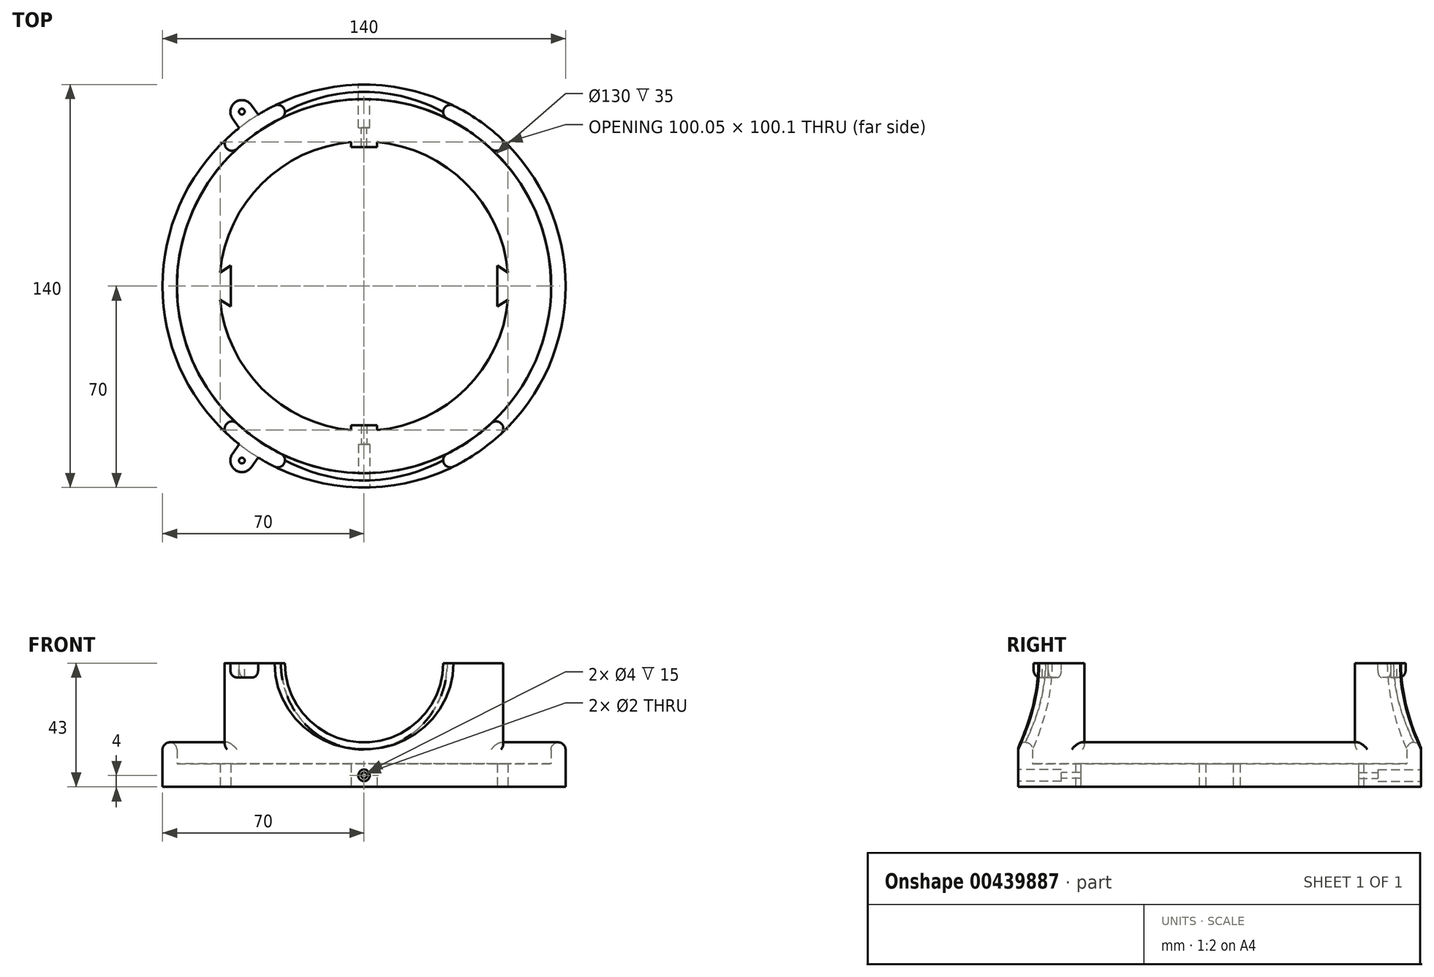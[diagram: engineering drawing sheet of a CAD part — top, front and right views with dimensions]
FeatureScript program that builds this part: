
annotation { "Feature Type Name" : "Feature", "Feature Type Description" : "" }
export const myFeature = defineFeature(function(context is Context, id is Id, definition is map)
    precondition{}
    {
        {
            var Q0;
            Q0=qCreatedBy(makeId("Top.planeOp"),FACE);
            var sketch = newSketch(context, id + "F0", { "sketchPlane" : qUnion([Q0])});
            skArc(sketch, "E0", {"start": v(-50.02, -4.77) * mm, "mid": v(-35.44, -35.63) * mm, "end": v(-4.5, -50.05) * mm});
            skCircle(sketch, "E1", {"center": v(0, 0) * mm, "radius": 70 * mm});
            skLineSegment(sketch, "E2.2.0.2", {"start": v(4.5, 50.05) * mm, "end": v(4.5, 48.3) * mm});
            skLineSegment(sketch, "E2.2.0.3", {"start": v(-4.5, 50.05) * mm, "end": v(-4.5, 48.3) * mm});
            skArc(sketch, "E3.trimOffspring", {"start": v(-4.5, 50.05) * mm, "mid": v(-35.44, 35.63) * mm, "end": v(-50.02, 4.77) * mm});
            skLineSegment(sketch, "E4", {"start": v(-4.5, 48.3) * mm, "end": v(4.5, 48.3) * mm});
            skLineSegment(sketch, "E5.MirrorCS", {"start": v(-4.5, -50.05) * mm, "end": v(-4.5, -48.3) * mm});
            skLineSegment(sketch, "E6.MirrorCS", {"start": v(4.5, -50.05) * mm, "end": v(4.5, -48.3) * mm});
            skLineSegment(sketch, "E7.MirrorCS", {"start": v(-4.5, -48.3) * mm, "end": v(4.5, -48.3) * mm});
            skLineSegment(sketch, "E8", {"start": v(-46.3, 7.1) * mm, "end": v(-46.3, -7.1) * mm});
            skLineSegment(sketch, "E9", {"start": v(-50.02, -4.77) * mm, "end": v(-46.3, -7.1) * mm});
            skLineSegment(sketch, "E10", {"start": v(-50.02, 4.77) * mm, "end": v(-46.3, 7.1) * mm});
            skLineSegment(sketch, "E11.MirrorCS", {"start": v(50.02, -4.77) * mm, "end": v(46.3, -7.1) * mm});
            skLineSegment(sketch, "E12.MirrorCS", {"start": v(50.02, 4.77) * mm, "end": v(46.3, 7.1) * mm});
            skLineSegment(sketch, "E13.MirrorCS", {"start": v(46.3, 7.1) * mm, "end": v(46.3, -7.1) * mm});
            skArc(sketch, "E14.MirrorCS", {"start": v(4.5, 50.05) * mm, "mid": v(35.44, 35.63) * mm, "end": v(50.02, 4.77) * mm});
            skArc(sketch, "E15.MirrorCS", {"start": v(50.02, -4.77) * mm, "mid": v(35.44, -35.63) * mm, "end": v(4.5, -50.05) * mm});
            skSolve(sketch);
        }
        {
            var Q0;
            Q0=qSketchRegion(id+"F0",true);
            extrude(context, id + "F1", {"entities" : qUnion([Q0]), "depth" : 43 * mm});
        }
        {
            var Q0;
            Q0=qCreatedBy(makeId("Front.planeOp"),FACE);
            var sketch = newSketch(context, id + "F2", { "sketchPlane" : qUnion([Q0])});
            skCircle(sketch, "E16", {"center": v(0, 43) * mm, "radius": 27.5 * mm});
            skLineSegment(sketch, "E17", {"start": v(0, 0) * mm, "end": v(0, 43) * mm});
            skSolve(sketch);
        }
        {
            var Q0;
            Q0=qSketchRegion(id+"F2",true);
            extrude(context, id + "F3", {"entities" : qUnion([Q0]), "operationType" : NewBodyOperationType.REMOVE, "endBound" : BoundingType.SYMMETRIC, "oppositeDirection" : true, "depth" : 162.8 * mm});
        }
        {
            var Q0;
            Q0=makeQuery(id+"F1.opExtrude","CAP_FACE",FACE,{"disambiguationData":[OSD([sQuery(id+"F0.wireOp",EDGE,"E0"),sQuery(id+"F0.wireOp",EDGE,"E1"),sQuery(id+"F0.wireOp",EDGE,"KXo9hoNV-a9ZN-jEZJ-Yrdq-8QQVipn73RV8.bottom"),sQuery(id+"F0.wireOp",EDGE,"KXo9hoNV-a9ZN-jEZJ-Yrdq-8QQVipn73RV8.top"),sQuery(id+"F0.wireOp",EDGE,"KXo9hoNV-a9ZN-jEZJ-Yrdq-8QQVipn73RV8.right"),sQuery(id+"F0.wireOp",EDGE,"E2.1.0.1"),sQuery(id+"F0.wireOp",EDGE,"E2.1.0.2"),sQuery(id+"F0.wireOp",EDGE,"E2.1.0.3"),sQuery(id+"F0.wireOp",EDGE,"E2.2.0.0"),sQuery(id+"F0.wireOp",EDGE,"E2.2.0.2"),sQuery(id+"F0.wireOp",EDGE,"E2.2.0.3"),sQuery(id+"F0.wireOp",EDGE,"E2.3.0.1"),sQuery(id+"F0.wireOp",EDGE,"E2.3.0.2"),sQuery(id+"F0.wireOp",EDGE,"E2.3.0.3"),sQuery(id+"F0.wireOp",EDGE,"085ecb79-89d6-48a0-bd8e-482740248965.trimOffspring"),sQuery(id+"F0.wireOp",EDGE,"85cd406b-6394-40b1-ac36-b08ea9fcf00d.trimOffspring"),sQuery(id+"F0.wireOp",EDGE,"E3.trimOffspring")])],"isStart":false});
            var sketch = newSketch(context, id + "F4", { "sketchPlane" : qUnion([Q0])});
            skLineSegment(sketch, "E18", {"start": v(-70, 0) * mm, "end": v(70, 0) * mm, "construction": true});
            skLineSegment(sketch, "E19", {"start": v(60.95, -87.04) * mm, "end": v(0, 0) * mm, "construction": true});
            skLineSegment(sketch, "E20", {"start": v(-59.95, -85.62) * mm, "end": v(0, 0) * mm, "construction": true});
            skLineSegment(sketch, "E21", {"start": v(-55.05, 78.61) * mm, "end": v(0, 0) * mm, "construction": true});
            skLineSegment(sketch, "E22", {"start": v(60.26, 86.06) * mm, "end": v(0, 0) * mm, "construction": true});
            skCircle(sketch, "E23", {"center": v(-42.44, -60.62) * mm, "radius": 1 * mm, "construction": true});
            skCircle(sketch, "E24", {"center": v(0, 0) * mm, "radius": 70 * mm, "construction": true});
            skLineSegment(sketch, "E25", {"start": v(0, 68.4) * mm, "end": v(0, -71.35) * mm, "construction": true});
            skCircle(sketch, "E26.MirrorC", {"center": v(42.44, -60.62) * mm, "radius": 1 * mm, "construction": true});
            skCircle(sketch, "E27.MirrorC", {"center": v(42.44, 60.62) * mm, "radius": 1 * mm, "construction": true});
            skLineSegment(sketch, "E28.MirrorCS", {"start": v(39.17, 62.91) * mm, "end": v(36.68, 59.61) * mm});
            skCircle(sketch, "E29.MirrorC", {"center": v(-42.44, 60.62) * mm, "radius": 1 * mm, "construction": true});
            skArc(sketch, "E30", {"start": v(45.72, 58.32) * mm, "mid": v(44.74, 63.9) * mm, "end": v(39.17, 62.91) * mm});
            skLineSegment(sketch, "E31.MirrorCS", {"start": v(45.72, 58.32) * mm, "end": v(43.47, 54.86) * mm});
            skArc(sketch, "E32", {"start": v(-39.17, 62.91) * mm, "mid": v(-44.74, 63.9) * mm, "end": v(-45.72, 58.32) * mm});
            skLineSegment(sketch, "E33", {"start": v(-45.72, 58.32) * mm, "end": v(-43.36, 54.95) * mm});
            skLineSegment(sketch, "E34.MirrorCS", {"start": v(-39.17, 62.91) * mm, "end": v(-36.8, 59.54) * mm});
            skArc(sketch, "E35", {"start": v(39.17, -62.91) * mm, "mid": v(44.74, -63.9) * mm, "end": v(45.72, -58.32) * mm});
            skLineSegment(sketch, "E36", {"start": v(45.72, -58.32) * mm, "end": v(43.36, -54.95) * mm});
            skLineSegment(sketch, "E37.MirrorCS", {"start": v(39.17, -62.91) * mm, "end": v(36.8, -59.54) * mm});
            skArc(sketch, "E38", {"start": v(-45.72, -58.32) * mm, "mid": v(-44.74, -63.9) * mm, "end": v(-39.17, -62.91) * mm});
            skLineSegment(sketch, "E39", {"start": v(-45.72, -58.32) * mm, "end": v(-43.36, -54.95) * mm});
            skLineSegment(sketch, "E40.MirrorCS", {"start": v(-39.17, -62.91) * mm, "end": v(-36.8, -59.54) * mm});
            skSolve(sketch);
        }
        {
            var Q0;
            Q0=qSketchRegion(id+"F2",true);
            extrude(context, id + "F5", {"entities" : qUnion([Q0]), "operationType" : NewBodyOperationType.REMOVE, "endBound" : BoundingType.SYMMETRIC, "oppositeDirection" : true, "depth" : 172.6 * mm});
        }
        {
            var Q0;
            Q0=qCreatedBy(makeId("Right.planeOp"),FACE);
            var sketch = newSketch(context, id + "F6", { "sketchPlane" : qUnion([Q0])});
            skLineSegment(sketch, "E41.bottom", {"start": v(-47, 115.5) * mm, "end": v(47, 115.5) * mm});
            skLineSegment(sketch, "E41.top", {"start": v(-47, 15.5) * mm, "end": v(47, 15.5) * mm});
            skLineSegment(sketch, "E41.left", {"start": v(-47, 115.5) * mm, "end": v(-47, 15.5) * mm});
            skLineSegment(sketch, "E41.right", {"start": v(47, 115.5) * mm, "end": v(47, 15.5) * mm});
            skLineSegment(sketch, "E42", {"start": v(0, 0) * mm, "end": v(0, 15.5) * mm, "construction": true});
            skSolve(sketch);
        }
        {
            var Q0;
            Q0=qSketchRegion(id+"F6",true);
            extrude(context, id + "F7", {"entities" : qUnion([Q0]), "operationType" : NewBodyOperationType.REMOVE, "endBound" : BoundingType.SYMMETRIC, "depth" : 182.4 * mm});
        }
        {
            var Q0;
            Q0=makeQuery(id+"F1.opExtrude","CAP_FACE",FACE,{"disambiguationData":[OSD([sQuery(id+"F0.wireOp",EDGE,"E0"),sQuery(id+"F0.wireOp",EDGE,"E1"),sQuery(id+"F0.wireOp",EDGE,"E2.2.0.0"),sQuery(id+"F0.wireOp",EDGE,"E2.2.0.2"),sQuery(id+"F0.wireOp",EDGE,"E2.2.0.3"),sQuery(id+"F0.wireOp",EDGE,"E2.3.0.1"),sQuery(id+"F0.wireOp",EDGE,"E2.3.0.2"),sQuery(id+"F0.wireOp",EDGE,"E2.3.0.3"),sQuery(id+"F0.wireOp",EDGE,"085ecb79-89d6-48a0-bd8e-482740248965.trimOffspring"),sQuery(id+"F0.wireOp",EDGE,"85cd406b-6394-40b1-ac36-b08ea9fcf00d.trimOffspring"),sQuery(id+"F0.wireOp",EDGE,"E3.trimOffspring"),sQuery(id+"F0.wireOp",EDGE,"0wMoWTtO-hKPG-dmUJ-9eZK-Rki3Ka56Pj0p"),sQuery(id+"F0.wireOp",EDGE,"V7nILoa6-agM4-B80q-80k6-MabAC6LeFQ3d"),sQuery(id+"F0.wireOp",EDGE,"T4tWseir-YMXC-WR8s-1T1N-fBKYRdHiWXzI"),sQuery(id+"F0.wireOp",EDGE,"GhSFunWE-UcgT-IK5w-9III-MmuMwgvZ9d2i"),sQuery(id+"F0.wireOp",EDGE,"6XujKZao-lyGk-p0ZG-WLlf-O7pdLShlOZ0q"),sQuery(id+"F0.wireOp",EDGE,"wTnajsCB-XfUZ-x2k5-9YjB-GDWOXe4ybcG3")])],"isStart":true});
            cPlane(context, id + "F8", {"entities" : qUnion([Q0]), "cplaneType" : CPlaneType.OFFSET, "offset" : 8 * mm, "oppositeDirection" : true, "width" : 150 * mm, "height" : 150 * mm});
        }
        {
            var Q0;
            Q0=qCreatedBy(id+"F8.planeOp",FACE);
            var sketch = newSketch(context, id + "F9", { "sketchPlane" : qUnion([Q0])});
            skCircle(sketch, "E43", {"center": v(0, 0) * mm, "radius": 50.25 * mm});
            skSolve(sketch);
        }
        {
            var Q0;
            Q0=qSketchRegion(id+"F9",true);
            var Q1;
            Q1=sQuery(id+"F9.wireOp",EDGE,"E43");
            extrude(context, id + "F10", {"entities" : qUnion([Q0]), "operationType" : NewBodyOperationType.REMOVE, "surfaceEntities" : qUnion([Q1]), "oppositeDirection" : true, "depth" : 73.1 * mm});
        }
        {
            var Q0;
            Q0=makeQuery(id+"F4.imprint","IMPRINT",FACE,{"disambiguationData":[TD([[makeQuery(id+"F4.imprint","IMPRINT",EDGE,{"derivedFrom":sQuery(id+"F4.wireOp",EDGE,"E32")}),1.0]])]});
            var Q1;
            {var subQ0=sQuery(id+"F4.wireOp",EDGE,"E30");Q1=makeQuery(id+"F4.imprint","IMPRINT",FACE,{"disambiguationData":[TD([[makeQuery(id+"F4.imprint","IMPRINT",EDGE,{"derivedFrom":subQ0}),1.0]])]});}
            var Q2;
            Q2=makeQuery(id+"F4.imprint","IMPRINT",FACE,{"disambiguationData":[TD([[makeQuery(id+"F4.imprint","IMPRINT",EDGE,{"derivedFrom":sQuery(id+"F4.wireOp",EDGE,"E35")}),1.0]])]});
            var Q3;
            Q3=makeQuery(id+"F4.imprint","IMPRINT",FACE,{"disambiguationData":[TD([[makeQuery(id+"F4.imprint","IMPRINT",EDGE,{"derivedFrom":sQuery(id+"F4.wireOp",EDGE,"E38")}),1.0]])]});
            extrude(context, id + "F11", {"entities" : qUnion([Q0, Q1, Q2, Q3]), "operationType" : NewBodyOperationType.ADD, "oppositeDirection" : true, "depth" : 5 * mm});
        }
        {
            var Q0;
            Q0=sQuery(id+"F4.wireOp",VERTEX,"E29.MirrorC.center");
            var Q1;
            Q1=sQuery(id+"F4.wireOp",VERTEX,"E30.center");
            var Q2;
            Q2=sQuery(id+"F4.wireOp",VERTEX,"E35.center");
            var Q3;
            Q3=sQuery(id+"F4.wireOp",VERTEX,"E23.center");
            var Q4;
            Q4=makeQuery(id+"F1.opExtrude","SWEPT_BODY",BODY,{"disambiguationData":[OSD([sQuery(id+"F0.wireOp",EDGE,"E0"),sQuery(id+"F0.wireOp",EDGE,"E1"),sQuery(id+"F0.wireOp",EDGE,"E2.2.0.2"),sQuery(id+"F0.wireOp",EDGE,"E2.2.0.3"),sQuery(id+"F0.wireOp",EDGE,"085ecb79-89d6-48a0-bd8e-482740248965.trimOffspring"),sQuery(id+"F0.wireOp",EDGE,"85cd406b-6394-40b1-ac36-b08ea9fcf00d.trimOffspring"),sQuery(id+"F0.wireOp",EDGE,"E3.trimOffspring"),sQuery(id+"F0.wireOp",EDGE,"wPdThzp9-JF6t-tdpl-VHkU-ta3l5vbWA5lS"),sQuery(id+"F0.wireOp",EDGE,"bCEz1Pkn-wXIZ-K7jB-S2CN-AWV0JzSdVKlh"),sQuery(id+"F0.wireOp",EDGE,"JKQ4kFbc-aIyo-4Fwi-89Tz-roniWSClhzpP"),sQuery(id+"F0.wireOp",EDGE,"de4d509a-07cf-4a36-b25b-d70c5453503e0.MirrorCS"),sQuery(id+"F0.wireOp",EDGE,"de4d509a-07cf-4a36-b25b-d70c5453503e1.MirrorCS"),sQuery(id+"F0.wireOp",EDGE,"de4d509a-07cf-4a36-b25b-d70c5453503e2.MirrorCS"),sQuery(id+"F0.wireOp",EDGE,"E4"),sQuery(id+"F0.wireOp",EDGE,"E5.MirrorCS"),sQuery(id+"F0.wireOp",EDGE,"E6.MirrorCS"),sQuery(id+"F0.wireOp",EDGE,"E7.MirrorCS")])]});
            hole(context, id + "F12", {"style" : HoleStyle.SIMPLE, "endStyle" : HoleEndStyle.BLIND, "holeDiameter" : 2 * mm, "holeDepth" : 5 * mm, "isTappedThrough" : true, "tappedDepth" : 12 * mm, "tapClearance" : 3, "startFromSketch" : true, "locations" : qUnion([Q0, Q1, Q2, Q3]), "scope" : qUnion([Q4])});
        }
        {
            var Q0;
            Q0=qCreatedBy(makeId("Top.planeOp"),FACE);
            cPlane(context, id + "F13", {"entities" : qUnion([Q0]), "cplaneType" : CPlaneType.OFFSET, "offset" : 8 * mm, "width" : 150 * mm, "height" : 150 * mm});
        }
        {
            var Q0;
            Q0=qCreatedBy(id+"F13.planeOp",FACE);
            var sketch = newSketch(context, id + "F14", { "sketchPlane" : qUnion([Q0])});
            skCircle(sketch, "E44", {"center": v(0, 0) * mm, "radius": 65 * mm});
            skCircle(sketch, "E45", {"center": v(0, 0) * mm, "radius": 50.25 * mm});
            skSolve(sketch);
        }
        {
            var Q0;
            Q0 = qSketchRegion(id + "F14", true);
            extrude(context, id + "F15", {"entities" : qUnion([Q0]), "operationType" : NewBodyOperationType.REMOVE, "depth" : 63.8 * mm});
        }
        {
            var Q0;
            Q0=makeQuery(id+"F7.boolean.opBoolean","INTERSECT",EDGE,{"disambiguationData":[OD(1.0)],"derivedFrom":[makeQuery(id+"F1.opExtrude","SWEPT_FACE",FACE,{"disambiguationData":[OSD([sQuery(id+"F0.wireOp",EDGE,"E1")])]}),makeQuery(id+"F7.opExtrude","SWEPT_FACE",FACE,{"disambiguationData":[OSD([sQuery(id+"F6.wireOp",EDGE,"E41.top")])]})]});
            var Q1;
            Q1=makeQuery(id+"F7.boolean.opBoolean","INTERSECT",EDGE,{"disambiguationData":[OD(0.0)],"derivedFrom":[makeQuery(id+"F1.opExtrude","SWEPT_FACE",FACE,{"disambiguationData":[OSD([sQuery(id+"F0.wireOp",EDGE,"E1")])]}),makeQuery(id+"F7.opExtrude","SWEPT_FACE",FACE,{"disambiguationData":[OSD([sQuery(id+"F6.wireOp",EDGE,"E41.top")])]})]});
            var Q2;
            Q2=makeQuery(id+"F3.boolean.opBoolean","INTERSECT",EDGE,{"disambiguationData":[OD(0.0)],"derivedFrom":[makeQuery(id+"F1.opExtrude","SWEPT_FACE",FACE,{"disambiguationData":[OSD([sQuery(id+"F0.wireOp",EDGE,"E1")])]}),makeQuery(id+"F3.opExtrude","SWEPT_FACE",FACE,{"disambiguationData":[OSD([sQuery(id+"F2.wireOp",EDGE,"E16")])]})]});
            var Q3;
            Q3=makeQuery(id+"F3.boolean.opBoolean","INTERSECT",EDGE,{"disambiguationData":[OD(1.0)],"derivedFrom":[makeQuery(id+"F1.opExtrude","SWEPT_FACE",FACE,{"disambiguationData":[OSD([sQuery(id+"F0.wireOp",EDGE,"E1")])]}),makeQuery(id+"F3.opExtrude","SWEPT_FACE",FACE,{"disambiguationData":[OSD([sQuery(id+"F2.wireOp",EDGE,"E16")])]})]});
            var Q4;
            {var subQ5=sQuery(id+"F0.wireOp",EDGE,"E0");Q4=makeQuery(id+"F15.boolean.opBoolean","INTERSECT",EDGE,{"derivedFrom":[makeQuery(id+"F3.boolean.opBoolean","COPY",FACE,{"disambiguationData":[TD([makeQuery(id+"F1.opExtrude","SWEPT_FACE",FACE,{"disambiguationData":[OSD([subQ5])]})])],"derivedFrom":makeQuery(id+"F3.opExtrude","SWEPT_FACE",FACE,{"disambiguationData":[OSD([sQuery(id+"F2.wireOp",EDGE,"E16")])]})}),makeQuery(id+"F15.opExtrude","SWEPT_FACE",FACE,{"disambiguationData":[OSD([sQuery(id+"F14.wireOp",EDGE,"E44")])]})]});}
            var Q5;
            {var subQ1=sQuery(id+"F0.wireOp",EDGE,"E2.2.0.2");Q5=makeQuery(id+"F15.boolean.opBoolean","INTERSECT",EDGE,{"derivedFrom":[makeQuery(id+"F3.boolean.opBoolean","COPY",FACE,{"disambiguationData":[TD([makeQuery(id+"F1.opExtrude","SWEPT_FACE",FACE,{"disambiguationData":[OSD([subQ1])]})])],"derivedFrom":makeQuery(id+"F3.opExtrude","SWEPT_FACE",FACE,{"disambiguationData":[OSD([sQuery(id+"F2.wireOp",EDGE,"E16")])]})}),makeQuery(id+"F15.opExtrude","SWEPT_FACE",FACE,{"disambiguationData":[OSD([sQuery(id+"F14.wireOp",EDGE,"E44")])]})]});}
            var Q6;
            Q6=makeQuery(id+"F15.boolean.opBoolean","INTERSECT",EDGE,{"derivedFrom":[makeQuery(id+"F7.boolean.opBoolean","COPY",FACE,{"disambiguationData":[TD([makeQuery(id+"F1.opExtrude","SWEPT_FACE",FACE,{"disambiguationData":[OSD([sQuery(id+"F0.wireOp",EDGE,"E11.MirrorCS")])]})])],"derivedFrom":makeQuery(id+"F7.opExtrude","SWEPT_FACE",FACE,{"disambiguationData":[OSD([sQuery(id+"F6.wireOp",EDGE,"E41.top")])]})}),makeQuery(id+"F15.opExtrude","SWEPT_FACE",FACE,{"disambiguationData":[OSD([sQuery(id+"F14.wireOp",EDGE,"E44")])]})]});
            var Q7;
            Q7=makeQuery(id+"F15.boolean.opBoolean","INTERSECT",EDGE,{"derivedFrom":[makeQuery(id+"F7.boolean.opBoolean","COPY",FACE,{"disambiguationData":[TD([makeQuery(id+"F1.opExtrude","SWEPT_FACE",FACE,{"disambiguationData":[OSD([sQuery(id+"F0.wireOp",EDGE,"E0")])]})])],"derivedFrom":makeQuery(id+"F7.opExtrude","SWEPT_FACE",FACE,{"disambiguationData":[OSD([sQuery(id+"F6.wireOp",EDGE,"E41.top")])]})}),makeQuery(id+"F15.opExtrude","SWEPT_FACE",FACE,{"disambiguationData":[OSD([sQuery(id+"F14.wireOp",EDGE,"E44")])]})]});
            fillet(context, id + "F16", {"entities" : qUnion([Q0, Q1, Q2, Q3, Q4, Q5, Q6, Q7]), "radius" : 2.5 * mm, "tangentPropagation" : true, "allowEdgeOverflow" : false});
        }
        {
            var Q0;
            {var subQ3=sQuery(id+"F0.wireOp",EDGE,"E15.MirrorCS");var subQ8=makeQuery(id+"F1.opExtrude","SWEPT_FACE",FACE,{"disambiguationData":[OSD([subQ3])]});Q0=makeQuery(id+"F15.boolean.opBoolean","INTERSECT",EDGE,{"derivedFrom":[makeQuery(id+"F7.boolean.opBoolean","COPY",FACE,{"disambiguationData":[TD([subQ8])],"derivedFrom":makeQuery(id+"F7.opExtrude","SWEPT_FACE",FACE,{"disambiguationData":[OSD([sQuery(id+"F6.wireOp",EDGE,"E41.left")])]})}),makeQuery(id+"F15.opExtrude","SWEPT_FACE",FACE,{"disambiguationData":[OSD([sQuery(id+"F14.wireOp",EDGE,"E44")])]})]});}
            var Q1;
            {var subQ4=sQuery(id+"F0.wireOp",EDGE,"E14.MirrorCS");var subQ8=makeQuery(id+"F1.opExtrude","SWEPT_FACE",FACE,{"disambiguationData":[OSD([subQ4])]});Q1=makeQuery(id+"F15.boolean.opBoolean","INTERSECT",EDGE,{"derivedFrom":[makeQuery(id+"F7.boolean.opBoolean","COPY",FACE,{"disambiguationData":[TD([subQ8])],"derivedFrom":makeQuery(id+"F7.opExtrude","SWEPT_FACE",FACE,{"disambiguationData":[OSD([sQuery(id+"F6.wireOp",EDGE,"E41.right")])]})}),makeQuery(id+"F15.opExtrude","SWEPT_FACE",FACE,{"disambiguationData":[OSD([sQuery(id+"F14.wireOp",EDGE,"E44")])]})]});}
            var Q2;
            {var subQ5=sQuery(id+"F0.wireOp",EDGE,"E0");Q2=makeQuery(id+"F15.boolean.opBoolean","INTERSECT",EDGE,{"derivedFrom":[makeQuery(id+"F3.boolean.opBoolean","COPY",FACE,{"disambiguationData":[TD([makeQuery(id+"F1.opExtrude","SWEPT_FACE",FACE,{"disambiguationData":[OSD([subQ5])]})])],"derivedFrom":makeQuery(id+"F3.opExtrude","SWEPT_FACE",FACE,{"disambiguationData":[OSD([sQuery(id+"F2.wireOp",EDGE,"E16")])]})}),makeQuery(id+"F15.opExtrude","SWEPT_FACE",FACE,{"disambiguationData":[OSD([sQuery(id+"F14.wireOp",EDGE,"E44")])]})]});}
            var Q3;
            Q3=makeQuery(id+"F7.boolean.opBoolean","INTERSECT",EDGE,{"disambiguationData":[OD(1.0)],"derivedFrom":[makeQuery(id+"F1.opExtrude","SWEPT_FACE",FACE,{"disambiguationData":[OSD([sQuery(id+"F0.wireOp",EDGE,"E1")])]}),makeQuery(id+"F7.opExtrude","SWEPT_FACE",FACE,{"disambiguationData":[OSD([sQuery(id+"F6.wireOp",EDGE,"E41.right")])]})]});
            var Q4;
            Q4=makeQuery(id+"F7.boolean.opBoolean","INTERSECT",EDGE,{"disambiguationData":[OD(1.0)],"derivedFrom":[makeQuery(id+"F1.opExtrude","SWEPT_FACE",FACE,{"disambiguationData":[OSD([sQuery(id+"F0.wireOp",EDGE,"E1")])]}),makeQuery(id+"F7.opExtrude","SWEPT_FACE",FACE,{"disambiguationData":[OSD([sQuery(id+"F6.wireOp",EDGE,"E41.left")])]})]});
            var Q5;
            Q5=makeQuery(id+"F7.boolean.opBoolean","INTERSECT",EDGE,{"disambiguationData":[OD(0.0)],"derivedFrom":[makeQuery(id+"F1.opExtrude","SWEPT_FACE",FACE,{"disambiguationData":[OSD([sQuery(id+"F0.wireOp",EDGE,"E1")])]}),makeQuery(id+"F7.opExtrude","SWEPT_FACE",FACE,{"disambiguationData":[OSD([sQuery(id+"F6.wireOp",EDGE,"E41.left")])]})]});
            var Q6;
            Q6=makeQuery(id+"F7.boolean.opBoolean","INTERSECT",EDGE,{"disambiguationData":[OD(0.0)],"derivedFrom":[makeQuery(id+"F1.opExtrude","SWEPT_FACE",FACE,{"disambiguationData":[OSD([sQuery(id+"F0.wireOp",EDGE,"E1")])]}),makeQuery(id+"F7.opExtrude","SWEPT_FACE",FACE,{"disambiguationData":[OSD([sQuery(id+"F6.wireOp",EDGE,"E41.right")])]})]});
            var Q7;
            {var subQ6=sQuery(id+"F0.wireOp",EDGE,"E0");var subQ8=makeQuery(id+"F1.opExtrude","SWEPT_FACE",FACE,{"disambiguationData":[OSD([subQ6])]});Q7=makeQuery(id+"F15.boolean.opBoolean","INTERSECT",EDGE,{"derivedFrom":[makeQuery(id+"F7.boolean.opBoolean","COPY",FACE,{"disambiguationData":[TD([subQ8])],"derivedFrom":makeQuery(id+"F7.opExtrude","SWEPT_FACE",FACE,{"disambiguationData":[OSD([sQuery(id+"F6.wireOp",EDGE,"E41.left")])]})}),makeQuery(id+"F15.opExtrude","SWEPT_FACE",FACE,{"disambiguationData":[OSD([sQuery(id+"F14.wireOp",EDGE,"E44")])]})]});}
            var Q8;
            {var subQ6=sQuery(id+"F0.wireOp",EDGE,"E3.trimOffspring");var subQ8=makeQuery(id+"F1.opExtrude","SWEPT_FACE",FACE,{"disambiguationData":[OSD([subQ6])]});Q8=makeQuery(id+"F15.boolean.opBoolean","INTERSECT",EDGE,{"derivedFrom":[makeQuery(id+"F7.boolean.opBoolean","COPY",FACE,{"disambiguationData":[TD([subQ8])],"derivedFrom":makeQuery(id+"F7.opExtrude","SWEPT_FACE",FACE,{"disambiguationData":[OSD([sQuery(id+"F6.wireOp",EDGE,"E41.right")])]})}),makeQuery(id+"F15.opExtrude","SWEPT_FACE",FACE,{"disambiguationData":[OSD([sQuery(id+"F14.wireOp",EDGE,"E44")])]})]});}
            fillet(context, id + "F17", {"entities" : qUnion([Q0, Q1, Q2, Q3, Q4, Q5, Q6, Q7, Q8]), "radius" : 2.5 * mm, "tangentPropagation" : true, "allowEdgeOverflow" : false});
        }
        {
            var Q0;
            Q0=makeQuery(id+"F11.opExtrude","CAP_EDGE",EDGE,{"disambiguationData":[OSD([sQuery(id+"F4.wireOp",EDGE,"E38")])],"isStart":false});
            var Q1;
            Q1=makeQuery(id+"F11.opExtrude","CAP_EDGE",EDGE,{"disambiguationData":[OSD([sQuery(id+"F4.wireOp",EDGE,"E35")])],"isStart":false});
            var Q2;
            Q2=makeQuery(id+"F11.opExtrude","CAP_EDGE",EDGE,{"disambiguationData":[OSD([sQuery(id+"F4.wireOp",EDGE,"E30")])],"isStart":false});
            var Q3;
            Q3=makeQuery(id+"F11.opExtrude","CAP_EDGE",EDGE,{"disambiguationData":[OSD([sQuery(id+"F4.wireOp",EDGE,"E32")])],"isStart":false});
            fillet(context, id + "F18", {"entities" : qUnion([Q0, Q1, Q2, Q3]), "radius" : 2.5 * mm, "tangentPropagation" : true, "allowEdgeOverflow" : false});
        }
        {
            var Q0;
            Q0=qCreatedBy(makeId("Front.planeOp"),FACE);
            cPlane(context, id + "F19", {"entities" : qUnion([Q0]), "cplaneType" : CPlaneType.OFFSET, "offset" : 70 * mm, "width" : 150 * mm, "height" : 150 * mm});
        }
        {
            var Q0;
            Q0=qCreatedBy(id+"F19.planeOp",FACE);
            var sketch = newSketch(context, id + "F20", { "sketchPlane" : qUnion([Q0])});
            skCircle(sketch, "E46", {"center": v(0, 4) * mm, "radius": 1.42 * mm, "construction": true});
            skSolve(sketch);
        }
        {
            var Q0;
            Q0=sQuery(id+"F20.wireOp",VERTEX,"E46.center");
            var Q1;
            Q1=makeQuery(id+"F1.opExtrude","SWEPT_BODY",BODY,{"disambiguationData":[OSD([sQuery(id+"F0.wireOp",EDGE,"E0"),sQuery(id+"F0.wireOp",EDGE,"E1"),sQuery(id+"F0.wireOp",EDGE,"E2.2.0.2"),sQuery(id+"F0.wireOp",EDGE,"E2.2.0.3"),sQuery(id+"F0.wireOp",EDGE,"085ecb79-89d6-48a0-bd8e-482740248965.trimOffspring"),sQuery(id+"F0.wireOp",EDGE,"85cd406b-6394-40b1-ac36-b08ea9fcf00d.trimOffspring"),sQuery(id+"F0.wireOp",EDGE,"E3.trimOffspring"),sQuery(id+"F0.wireOp",EDGE,"wPdThzp9-JF6t-tdpl-VHkU-ta3l5vbWA5lS"),sQuery(id+"F0.wireOp",EDGE,"bCEz1Pkn-wXIZ-K7jB-S2CN-AWV0JzSdVKlh"),sQuery(id+"F0.wireOp",EDGE,"JKQ4kFbc-aIyo-4Fwi-89Tz-roniWSClhzpP"),sQuery(id+"F0.wireOp",EDGE,"de4d509a-07cf-4a36-b25b-d70c5453503e0.MirrorCS"),sQuery(id+"F0.wireOp",EDGE,"de4d509a-07cf-4a36-b25b-d70c5453503e1.MirrorCS"),sQuery(id+"F0.wireOp",EDGE,"de4d509a-07cf-4a36-b25b-d70c5453503e2.MirrorCS"),sQuery(id+"F0.wireOp",EDGE,"E4"),sQuery(id+"F0.wireOp",EDGE,"E5.MirrorCS"),sQuery(id+"F0.wireOp",EDGE,"E6.MirrorCS"),sQuery(id+"F0.wireOp",EDGE,"E7.MirrorCS")])]});
            hole(context, id + "F21", {"style" : HoleStyle.C_BORE, "endStyle" : HoleEndStyle.BLIND, "holeDiameter" : 2 * mm, "cBoreDiameter" : 4 * mm, "cBoreDepth" : 15 * mm, "holeDepth" : 22 * mm, "isTappedThrough" : true, "tappedDepth" : 12 * mm, "tapClearance" : 3, "startFromSketch" : true, "locations" : qUnion([Q0]), "scope" : qUnion([Q1])});
        }
        {
            var Q0;
            Q0=qCreatedBy(makeId("Front.planeOp"),FACE);
            cPlane(context, id + "F22", {"entities" : qUnion([Q0]), "cplaneType" : CPlaneType.OFFSET, "offset" : 70 * mm, "oppositeDirection" : true, "width" : 150 * mm, "height" : 150 * mm});
        }
        {
            var Q0;
            Q0=qCreatedBy(id+"F22.planeOp",FACE);
            var sketch = newSketch(context, id + "F23", { "sketchPlane" : qUnion([Q0])});
            skCircle(sketch, "E47", {"center": v(0, 4) * mm, "radius": 2.5 * mm, "construction": true});
            skSolve(sketch);
        }
        {
            var Q0;
            Q0=sQuery(id+"F23.wireOp",VERTEX,"E47.center");
            var Q1;
            Q1=makeQuery(id+"F1.opExtrude","SWEPT_BODY",BODY,{"disambiguationData":[OSD([sQuery(id+"F0.wireOp",EDGE,"E0"),sQuery(id+"F0.wireOp",EDGE,"E1"),sQuery(id+"F0.wireOp",EDGE,"E2.2.0.2"),sQuery(id+"F0.wireOp",EDGE,"E2.2.0.3"),sQuery(id+"F0.wireOp",EDGE,"085ecb79-89d6-48a0-bd8e-482740248965.trimOffspring"),sQuery(id+"F0.wireOp",EDGE,"85cd406b-6394-40b1-ac36-b08ea9fcf00d.trimOffspring"),sQuery(id+"F0.wireOp",EDGE,"E3.trimOffspring"),sQuery(id+"F0.wireOp",EDGE,"wPdThzp9-JF6t-tdpl-VHkU-ta3l5vbWA5lS"),sQuery(id+"F0.wireOp",EDGE,"bCEz1Pkn-wXIZ-K7jB-S2CN-AWV0JzSdVKlh"),sQuery(id+"F0.wireOp",EDGE,"JKQ4kFbc-aIyo-4Fwi-89Tz-roniWSClhzpP"),sQuery(id+"F0.wireOp",EDGE,"de4d509a-07cf-4a36-b25b-d70c5453503e0.MirrorCS"),sQuery(id+"F0.wireOp",EDGE,"de4d509a-07cf-4a36-b25b-d70c5453503e1.MirrorCS"),sQuery(id+"F0.wireOp",EDGE,"de4d509a-07cf-4a36-b25b-d70c5453503e2.MirrorCS"),sQuery(id+"F0.wireOp",EDGE,"E4"),sQuery(id+"F0.wireOp",EDGE,"E5.MirrorCS"),sQuery(id+"F0.wireOp",EDGE,"E6.MirrorCS"),sQuery(id+"F0.wireOp",EDGE,"E7.MirrorCS")])]});
            hole(context, id + "F24", {"style" : HoleStyle.C_BORE, "endStyle" : HoleEndStyle.BLIND, "oppositeDirection" : true, "holeDiameter" : 2 * mm, "cBoreDiameter" : 4 * mm, "cBoreDepth" : 15 * mm, "holeDepth" : 22 * mm, "isTappedThrough" : true, "tappedDepth" : 12 * mm, "tapClearance" : 3, "startFromSketch" : true, "locations" : qUnion([Q0]), "scope" : qUnion([Q1])});
        }
    });
